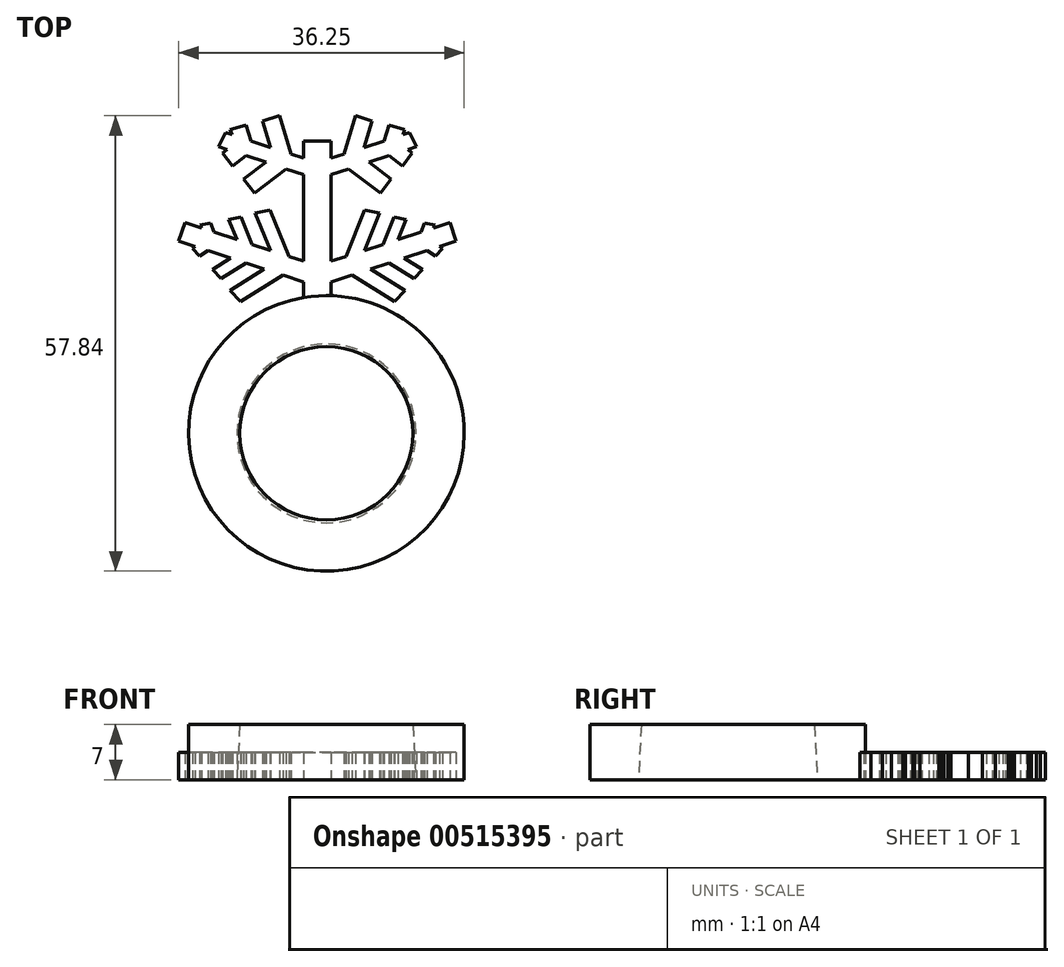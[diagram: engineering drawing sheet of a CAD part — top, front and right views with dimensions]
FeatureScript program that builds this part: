
annotation { "Feature Type Name" : "Feature", "Feature Type Description" : "" }
export const myFeature = defineFeature(function(context is Context, id is Id, definition is map)
    precondition{}
    {
        {
            var Q0;
            Q0=qCreatedBy(makeId("Top.planeOp"),FACE);
            var sketch = newSketch(context, id + "F0", { "sketchPlane" : qUnion([Q0])});
            skCircle(sketch, "E0", {"center": v(0, 0) * mm, "radius": 17.5 * mm});
            skSolve(sketch);
        }
        {
            var Q0;
            Q0=makeQuery(id+"F0.imprint","IMPRINT",FACE,{"disambiguationData":[TD([[makeQuery(id+"F0.imprint","IMPRINT",EDGE,{"derivedFrom":sQuery(id+"F0.wireOp",EDGE,"E0")}),1.0]])]});
            extrude(context, id + "F1", {"entities" : qUnion([Q0]), "depth" : 7 * mm, "offsetDistance" : 25 * mm});
        }
        {
            var Q0;
            Q0=makeQuery(id+"F1.opExtrude","CAP_FACE",FACE,{"disambiguationData":[OSD([sQuery(id+"F0.wireOp",EDGE,"E0")])],"isStart":false});
            var sketch = newSketch(context, id + "F2", { "sketchPlane" : qUnion([Q0])});
            skCircle(sketch, "E1", {"center": v(0, 0) * mm, "radius": 11 * mm});
            skSolve(sketch);
        }
        {
            var Q0;
            Q0=makeQuery(id+"F2.imprint","IMPRINT",FACE,{"disambiguationData":[TD([[makeQuery(id+"F2.imprint","IMPRINT",EDGE,{"derivedFrom":sQuery(id+"F2.wireOp",EDGE,"E1")}),1.0]])]});
            extrude(context, id + "F3", {"entities" : qUnion([Q0]), "operationType" : NewBodyOperationType.REMOVE, "endBound" : BoundingType.THROUGH_ALL, "oppositeDirection" : true, "depth" : 25 * mm, "offsetDistance" : 25 * mm, "hasDraft" : true, "draftAngle" : 3 * degree});
        }
        {
            var Q0;
            Q0=qCreatedBy(makeId("Top.planeOp"),FACE);
            var sketch = newSketch(context, id + "F4", { "sketchPlane" : qUnion([Q0])});
            skPoint(sketch, "E2", {"position": v(0, 38) * mm});
            skLineSegment(sketch, "E3", {"start": v(-2.88, 14.1) * mm, "end": v(0.62, 14.1) * mm});
            skLineSegment(sketch, "E4", {"start": v(0.62, 14.1) * mm, "end": v(0.62, 19.23) * mm});
            skLineSegment(sketch, "E5", {"start": v(-2.88, 14.1) * mm, "end": v(-2.88, 19.23) * mm});
            skLineSegment(sketch, "E6", {"start": v(-2.88, 37.14) * mm, "end": v(0.62, 37.14) * mm});
            skLineSegment(sketch, "E7", {"start": v(0.62, 19.23) * mm, "end": v(3.27, 20.1) * mm});
            skLineSegment(sketch, "E8", {"start": v(16.5, 24.4) * mm, "end": v(15.72, 26.78) * mm});
            skLineSegment(sketch, "E9", {"start": v(15.72, 26.78) * mm, "end": v(13.62, 26.1) * mm});
            skLineSegment(sketch, "E10", {"start": v(13.78, 26.47) * mm, "end": v(13.62, 26.1) * mm});
            skLineSegment(sketch, "E11", {"start": v(12.48, 26.73) * mm, "end": v(12, 25.57) * mm});
            skLineSegment(sketch, "E12", {"start": v(9.12, 24.63) * mm, "end": v(10.15, 27.16) * mm});
            skLineSegment(sketch, "E13", {"start": v(10.15, 27.16) * mm, "end": v(8.58, 27.47) * mm});
            skLineSegment(sketch, "E14", {"start": v(8.58, 27.47) * mm, "end": v(7.17, 24) * mm});
            skLineSegment(sketch, "E15", {"start": v(4.86, 23.24) * mm, "end": v(6.78, 27.97) * mm});
            skLineSegment(sketch, "E16", {"start": v(6.78, 27.97) * mm, "end": v(4.88, 28.34) * mm});
            skLineSegment(sketch, "E17", {"start": v(4.88, 28.34) * mm, "end": v(2.5, 22.47) * mm});
            skLineSegment(sketch, "E18", {"start": v(12.48, 26.73) * mm, "end": v(13.78, 26.47) * mm});
            skLineSegment(sketch, "E19.MirrorCS", {"start": v(8.65, 16.75) * mm, "end": v(3.27, 20.1) * mm});
            skLineSegment(sketch, "E20.MirrorCS", {"start": v(5.63, 20.86) * mm, "end": v(9.97, 18.17) * mm});
            skLineSegment(sketch, "E21.MirrorCS", {"start": v(9.97, 18.17) * mm, "end": v(8.65, 16.75) * mm});
            skLineSegment(sketch, "E22.MirrorCS", {"start": v(11.13, 19.64) * mm, "end": v(7.94, 21.62) * mm});
            skLineSegment(sketch, "E23.MirrorCS", {"start": v(9.9, 22.25) * mm, "end": v(12.22, 20.8) * mm});
            skLineSegment(sketch, "E24.MirrorCS", {"start": v(12.22, 20.8) * mm, "end": v(11.13, 19.64) * mm});
            skLineSegment(sketch, "E25.MirrorCS", {"start": v(13.84, 22.53) * mm, "end": v(12.78, 23.2) * mm});
            skLineSegment(sketch, "E26.MirrorCS", {"start": v(14.74, 23.5) * mm, "end": v(14.4, 23.72) * mm});
            skLineSegment(sketch, "E27.MirrorCS", {"start": v(13.84, 22.53) * mm, "end": v(14.74, 23.5) * mm});
            skLineSegment(sketch, "E28.trimOffspring", {"start": v(5.63, 20.86) * mm, "end": v(7.94, 21.62) * mm});
            skLineSegment(sketch, "E29.trimOffspring", {"start": v(2.5, 22.47) * mm, "end": v(0.62, 21.86) * mm});
            skLineSegment(sketch, "E30.trimOffspring", {"start": v(7.17, 24) * mm, "end": v(4.86, 23.24) * mm});
            skLineSegment(sketch, "E31.trimOffspring", {"start": v(9.9, 22.25) * mm, "end": v(12.78, 23.2) * mm});
            skLineSegment(sketch, "E32.trimOffspring", {"start": v(14.4, 23.72) * mm, "end": v(16.5, 24.4) * mm});
            skLineSegment(sketch, "E33.trimOffspring", {"start": v(12, 25.57) * mm, "end": v(9.12, 24.63) * mm});
            skLineSegment(sketch, "E34", {"start": v(0.62, 32.87) * mm, "end": v(2.84, 33.6) * mm});
            skLineSegment(sketch, "E35", {"start": v(0.62, 34.95) * mm, "end": v(2.23, 35.48) * mm});
            skLineSegment(sketch, "E36", {"start": v(2.23, 35.48) * mm, "end": v(3.7, 40.34) * mm});
            skLineSegment(sketch, "E37", {"start": v(3.7, 40.34) * mm, "end": v(5.83, 39.7) * mm});
            skLineSegment(sketch, "E38", {"start": v(5.83, 39.7) * mm, "end": v(4.81, 36.32) * mm});
            skLineSegment(sketch, "E39", {"start": v(7.34, 37.14) * mm, "end": v(7.96, 39.18) * mm});
            skLineSegment(sketch, "E40", {"start": v(7.96, 39.18) * mm, "end": v(9.94, 38.58) * mm});
            skLineSegment(sketch, "E41", {"start": v(9.94, 38.58) * mm, "end": v(9.75, 37.93) * mm});
            skLineSegment(sketch, "E42", {"start": v(10.56, 38.19) * mm, "end": v(11.45, 36.4) * mm});
            skLineSegment(sketch, "E43.MirrorCS", {"start": v(2.84, 33.6) * mm, "end": v(6.9, 30.53) * mm});
            skLineSegment(sketch, "E44.MirrorCS", {"start": v(6.9, 30.53) * mm, "end": v(8.24, 32.31) * mm});
            skLineSegment(sketch, "E45.MirrorCS", {"start": v(8.24, 32.31) * mm, "end": v(5.43, 34.44) * mm});
            skLineSegment(sketch, "E46.MirrorCS", {"start": v(7.96, 35.26) * mm, "end": v(9.65, 33.98) * mm});
            skLineSegment(sketch, "E47.MirrorCS", {"start": v(9.65, 33.98) * mm, "end": v(10.9, 35.63) * mm});
            skLineSegment(sketch, "E48.MirrorCS", {"start": v(10.9, 35.63) * mm, "end": v(10.36, 36.04) * mm});
            skLineSegment(sketch, "E49.trimOffspring", {"start": v(4.81, 36.32) * mm, "end": v(7.34, 37.14) * mm});
            skLineSegment(sketch, "E50.trimOffspring", {"start": v(9.75, 37.93) * mm, "end": v(10.56, 38.19) * mm});
            skLineSegment(sketch, "E51.trimOffspring", {"start": v(10.36, 36.04) * mm, "end": v(11.45, 36.4) * mm});
            skLineSegment(sketch, "E52.trimOffspring", {"start": v(5.43, 34.44) * mm, "end": v(7.96, 35.26) * mm});
            skLineSegment(sketch, "E53.MirrorCS", {"start": v(-2.88, 34.95) * mm, "end": v(-4.49, 35.48) * mm});
            skLineSegment(sketch, "E54.MirrorCS", {"start": v(-4.49, 35.48) * mm, "end": v(-5.95, 40.34) * mm});
            skLineSegment(sketch, "E55.MirrorCS", {"start": v(-5.95, 40.34) * mm, "end": v(-8.09, 39.7) * mm});
            skLineSegment(sketch, "E56.MirrorCS", {"start": v(-8.09, 39.7) * mm, "end": v(-7.07, 36.32) * mm});
            skLineSegment(sketch, "E57.MirrorCS", {"start": v(-9.6, 37.14) * mm, "end": v(-10.21, 39.18) * mm});
            skLineSegment(sketch, "E58.MirrorCS", {"start": v(-10.21, 39.18) * mm, "end": v(-12.2, 38.58) * mm});
            skLineSegment(sketch, "E59.MirrorCS", {"start": v(-12.2, 38.58) * mm, "end": v(-12, 37.93) * mm});
            skLineSegment(sketch, "E60.MirrorCS", {"start": v(-12, 37.93) * mm, "end": v(-12.81, 38.19) * mm});
            skLineSegment(sketch, "E61.MirrorCS", {"start": v(-7.07, 36.32) * mm, "end": v(-9.6, 37.14) * mm});
            skLineSegment(sketch, "E62.MirrorCS", {"start": v(-12.81, 38.19) * mm, "end": v(-13.7, 36.4) * mm});
            skLineSegment(sketch, "E63.MirrorCS", {"start": v(-12.62, 36.04) * mm, "end": v(-13.7, 36.4) * mm});
            skLineSegment(sketch, "E64.MirrorCS", {"start": v(-13.16, 35.63) * mm, "end": v(-12.62, 36.04) * mm});
            skLineSegment(sketch, "E65.MirrorCS", {"start": v(-11.9, 33.98) * mm, "end": v(-13.16, 35.63) * mm});
            skLineSegment(sketch, "E66.MirrorCS", {"start": v(-10.21, 35.26) * mm, "end": v(-11.9, 33.98) * mm});
            skLineSegment(sketch, "E67.MirrorCS", {"start": v(-7.68, 34.44) * mm, "end": v(-10.21, 35.26) * mm});
            skLineSegment(sketch, "E68.MirrorCS", {"start": v(-10.5, 32.31) * mm, "end": v(-7.68, 34.44) * mm});
            skLineSegment(sketch, "E69.MirrorCS", {"start": v(-9.15, 30.53) * mm, "end": v(-10.5, 32.31) * mm});
            skLineSegment(sketch, "E70.MirrorCS", {"start": v(-5.1, 33.6) * mm, "end": v(-9.15, 30.53) * mm});
            skLineSegment(sketch, "E71.MirrorCS", {"start": v(-2.88, 32.87) * mm, "end": v(-5.1, 33.6) * mm});
            skLineSegment(sketch, "E72.MirrorCS", {"start": v(-4.75, 22.47) * mm, "end": v(-2.88, 21.86) * mm});
            skLineSegment(sketch, "E73.MirrorCS", {"start": v(-7.13, 28.34) * mm, "end": v(-4.75, 22.47) * mm});
            skLineSegment(sketch, "E74.MirrorCS", {"start": v(-9.03, 27.97) * mm, "end": v(-7.13, 28.34) * mm});
            skLineSegment(sketch, "E75.MirrorCS", {"start": v(-7.12, 23.24) * mm, "end": v(-9.03, 27.97) * mm});
            skLineSegment(sketch, "E76.MirrorCS", {"start": v(-9.42, 24) * mm, "end": v(-7.12, 23.24) * mm});
            skLineSegment(sketch, "E77.MirrorCS", {"start": v(-10.83, 27.47) * mm, "end": v(-9.42, 24) * mm});
            skLineSegment(sketch, "E78.MirrorCS", {"start": v(-12.4, 27.16) * mm, "end": v(-10.83, 27.47) * mm});
            skLineSegment(sketch, "E79.MirrorCS", {"start": v(-11.38, 24.63) * mm, "end": v(-12.4, 27.16) * mm});
            skLineSegment(sketch, "E80.MirrorCS", {"start": v(-14.26, 25.57) * mm, "end": v(-11.38, 24.63) * mm});
            skLineSegment(sketch, "E81.MirrorCS", {"start": v(-14.73, 26.73) * mm, "end": v(-14.26, 25.57) * mm});
            skLineSegment(sketch, "E82.MirrorCS", {"start": v(-16.03, 26.47) * mm, "end": v(-15.88, 26.1) * mm});
            skLineSegment(sketch, "E83.MirrorCS", {"start": v(-17.98, 26.78) * mm, "end": v(-15.88, 26.1) * mm});
            skLineSegment(sketch, "E84.MirrorCS", {"start": v(-18.75, 24.4) * mm, "end": v(-17.98, 26.78) * mm});
            skLineSegment(sketch, "E85.MirrorCS", {"start": v(-16.65, 23.72) * mm, "end": v(-18.75, 24.4) * mm});
            skLineSegment(sketch, "E86.MirrorCS", {"start": v(-17, 23.5) * mm, "end": v(-16.65, 23.72) * mm});
            skLineSegment(sketch, "E87.MirrorCS", {"start": v(-16.1, 22.53) * mm, "end": v(-17, 23.5) * mm});
            skLineSegment(sketch, "E88.MirrorCS", {"start": v(-14.73, 26.73) * mm, "end": v(-16.03, 26.47) * mm});
            skLineSegment(sketch, "E89.MirrorCS", {"start": v(-14.48, 20.8) * mm, "end": v(-13.39, 19.64) * mm});
            skLineSegment(sketch, "E90.MirrorCS", {"start": v(-12.15, 22.25) * mm, "end": v(-14.48, 20.8) * mm});
            skLineSegment(sketch, "E91.MirrorCS", {"start": v(-12.15, 22.25) * mm, "end": v(-15.04, 23.2) * mm});
            skLineSegment(sketch, "E92.MirrorCS", {"start": v(-16.1, 22.53) * mm, "end": v(-15.04, 23.2) * mm});
            skLineSegment(sketch, "E93.MirrorCS", {"start": v(-13.39, 19.64) * mm, "end": v(-10.2, 21.62) * mm});
            skLineSegment(sketch, "E94.MirrorCS", {"start": v(-7.89, 20.86) * mm, "end": v(-10.2, 21.62) * mm});
            skLineSegment(sketch, "E95.MirrorCS", {"start": v(-7.89, 20.86) * mm, "end": v(-12.23, 18.17) * mm});
            skLineSegment(sketch, "E96.MirrorCS", {"start": v(-12.23, 18.17) * mm, "end": v(-10.91, 16.75) * mm});
            skLineSegment(sketch, "E97.MirrorCS", {"start": v(-10.91, 16.75) * mm, "end": v(-5.53, 20.1) * mm});
            skLineSegment(sketch, "E98.MirrorCS", {"start": v(-2.88, 19.23) * mm, "end": v(-5.53, 20.1) * mm});
            skLineSegment(sketch, "E99.trimOffspring", {"start": v(0.62, 21.86) * mm, "end": v(0.62, 32.87) * mm});
            skLineSegment(sketch, "E100.trimOffspring", {"start": v(-2.88, 21.86) * mm, "end": v(-2.88, 32.87) * mm});
            skPoint(sketch, "E101.start.orphan", {"position": v(16.1, 25.6) * mm});
            skPoint(sketch, "E102.end.orphan", {"position": v(-1.13, 14.1) * mm});
            skPoint(sketch, "E102.start.orphan", {"position": v(-1.13, 37.14) * mm});
            skLineSegment(sketch, "E103.trimOffspring", {"start": v(0.62, 34.95) * mm, "end": v(0.62, 37.14) * mm});
            skLineSegment(sketch, "E104.trimOffspring", {"start": v(-2.88, 34.95) * mm, "end": v(-2.88, 37.14) * mm});
            skPoint(sketch, "E105.start.orphan", {"position": v(11, 37.3) * mm});
            skSolve(sketch);
        }
        {
            var Q0;
            Q0=makeQuery(id+"F4.imprint","IMPRINT",FACE,{"disambiguationData":[TD([[makeQuery(id+"F4.imprint","IMPRINT",EDGE,{"derivedFrom":sQuery(id+"F4.wireOp",EDGE,"E3")}),1.0]])]});
            extrude(context, id + "F5", {"entities" : qUnion([Q0]), "operationType" : NewBodyOperationType.ADD, "depth" : (7 / 2) * mm, "offsetDistance" : 25 * mm});
        }
    });
